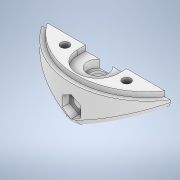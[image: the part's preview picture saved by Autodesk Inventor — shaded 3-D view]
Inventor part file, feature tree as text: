
AUTODESK INVENTOR PART (.ipt)
format: ipt  version: 2020 (Build 240168000, 168)  size: 334,336 bytes
history: native  units: in
note: dims shown in document units (in); Inventor stores cm internally (conversion verified against a paired STEP export)
features: sketch x7, extrude x3, revolve x2, fillet x2, hole x1
ambient origin geometry x8: Origin, YZ Plane, XZ Plane, XY Plane, X Axis, Y Axis, Z Axis, Center Point
bodies: Solid1 (feature_tree)
feature tree (15):
  sketch  "Sketch1"  dims[d2=1.745in d3=0.126in]
  revolve  "Revolution1"  [1 undecoded]
  extrude  "Extrusion1"  Depth=0.25in
  fillet  "Fillet1"  [1 undecoded]
  fillet  "Fillet2"  Radius=1.0in
  revolve  "Revolution2"  [1 undecoded]
  extrude  "Extrusion8"  Depth=1.5in
  extrude  "Extrusion9"  Depth=1.0in
  hole  "Hole5"  [1 undecoded]
  sketch  "Sketch2"  dims[d5=0.25in d7=0.25in d9=180.0deg d10=1.0in]
  sketch  "Sketch9"  dims[d11=1.85in d12=0.0in d16=1.382in d17=0.0in]
  sketch  "Sketch10"  dims[d46=1.25in d47=1.5in]
  sketch  "Sketch13"  dims[d48=0.205in d49=0.75in d50=0.3438in d51=0.5in d52=0.5635in d53=1.0in d54=0.8108in]
  sketch  "Sketch14"  dims[d55=0.266in d56=0.75in d57=0.875in d58=0.3125in d59=0.5635in d60=1.0in d61=0.8108in d65=0.0312in]
  sketch  "Sketch15"  dims[d66=0.125in d67=0.5in d78=90.0deg d91=0.4475in d92=0.1875in d93=0.0in d94=0.2in d95=0.0in d98=0.51in d108=0.5in d111=1.2in d112=0.35in d113=0.75in d114=0.51in d115=0.188in d116=0.5635in d117=0.25in d118=0.0in d119=1.85in d120=0.5in]
note: 4 required parameter values undecoded (feature->parameter linkage not recoverable at this tier; creation-order binding heuristic only, values carry confidence <= 0.55)